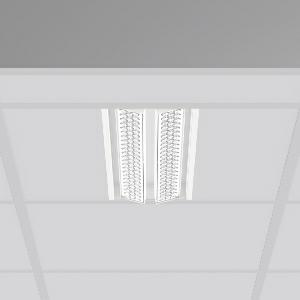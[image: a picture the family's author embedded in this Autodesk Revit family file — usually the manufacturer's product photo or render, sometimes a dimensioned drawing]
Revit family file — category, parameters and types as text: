
# Revit family: tx-move_901733_002_1_3693
name_source: partatom
category: Lighting Fixtures
units: mm (PartAtom-declared; Revit-internal decimal feet)

## family parameters
Cut with Voids When Loaded = No
Host = Face
Light Source = No
Part Type = Normal
Room Calculation Point = No
Round Connector Dimension = Use Diameter
Shared = No

## types (1)
- MultiLumen 1 (1 x LED Modul 840, 2850 lm, 4000)
    Apparent Load = 35 VA
    Approval mark = CE
    CIE Flux Codes = 77 96 99 100 100
    Color Rendering = 80
    Color Temperature = 4000
    Default Elevation = 1800 mm
    Description = Series: TX-MOVE
Einlege/Einbau-Flächenstrahler. Housing: sheet steel, powder-coated. 2xSwivel range: 90°. High-efficiency LED units with optimum light control thanks to clear plastic (PC) lens optics. Spezielle Mikrostrukturen reduzieren Gelbsaum. Symmetrical light distribution. Suitable for laying in grid ceiling module 600. Connected converter included in separate gearbox.Suitable for through-wiring.MultiLumen: Luminous flux adjustable in 3 steps. Accessories: Mounting frame for installation in suspended ceilings. Environmentally friendly and resource-saving due to replaceable and recyclable components. 
Colour: traffic white, matt (RAL 9016)
Length: 597 mm
Width: 190 mm
Height: 39 mm
Cut-out length: 577.5 mm
Cut-out width: 174 mm
Recess height: 100 mm
Lamp: LED
Socket: without socket
Colour temperature: 4000K
Colour rendering index (CRI): 80
System power: 35 W
Rated luminous flux: 5700 lm
Luminous efficiency: 163 lm/W
System power 2: 47 W
Rated luminous flux 2: 7450 lm
Luminous efficiency 2: 159 lm/W
System power 3: 68 W
Rated luminous flux 3: 10200 lm
Luminous efficiency 3: 150 lm/W
Control gear: Regulated power supply
Protection class: I
Type of protection: IP 20
    Height = 0 mm  [stored 0 ft]
    Lamp = 1 x LED Modul 840
    Lamp Light Flux = 2850 lm
    Lamp count = 1
    Length = 597 mm
    Lifetime = 50000 h
    Luminous efficacy = 163 lm/W
    Manufacturer = RZB
    ModVariant = No
    Model = 901733.002.1
    Mounting Place = Ceiling, Wall
    Mounting Type = Recessed
    Number of Poles = 1
    OnlyDefault = Yes
    Power Factor = 1
    Product Name = TX-MOVE
    Product group = Recessed projectors
    ProductGroupID = 401
    Protection Class = Protection class I
    Protection Degree = IP 20
    RLX_Detail_Level = 1
    RLX_Emergency_Light_Flux = 0 lm
    RLX_Emergency_Type = 0
    RLX_Emergency_Type_DB = No
    RlxData = <blob elided: 35373 chars, md5=a1c9b15f>
    Socket = socket
    Standby Power = 0 W
    System Light Flux = 5700 lm
    System Power = 35 W
    Type Comments = MultiLumen 1
    Type Image = 901733.002.jpg
    URL = http://relux.com
    VarID = multilumen_1
    Voltage = 230 V
    Voltage Range = 220-240 V
    Weight = 0.00 kg
    Width = 190 mm  [stored 0.62336 ft]

note: [stored X ft] marks values corroborated as IEEE doubles in the binary element streams (Revit-internal decimal feet)

## geometry (parser evidence)
native form markers: Blend x4, Sweep x14
no freeform markers — native parametric forms only
